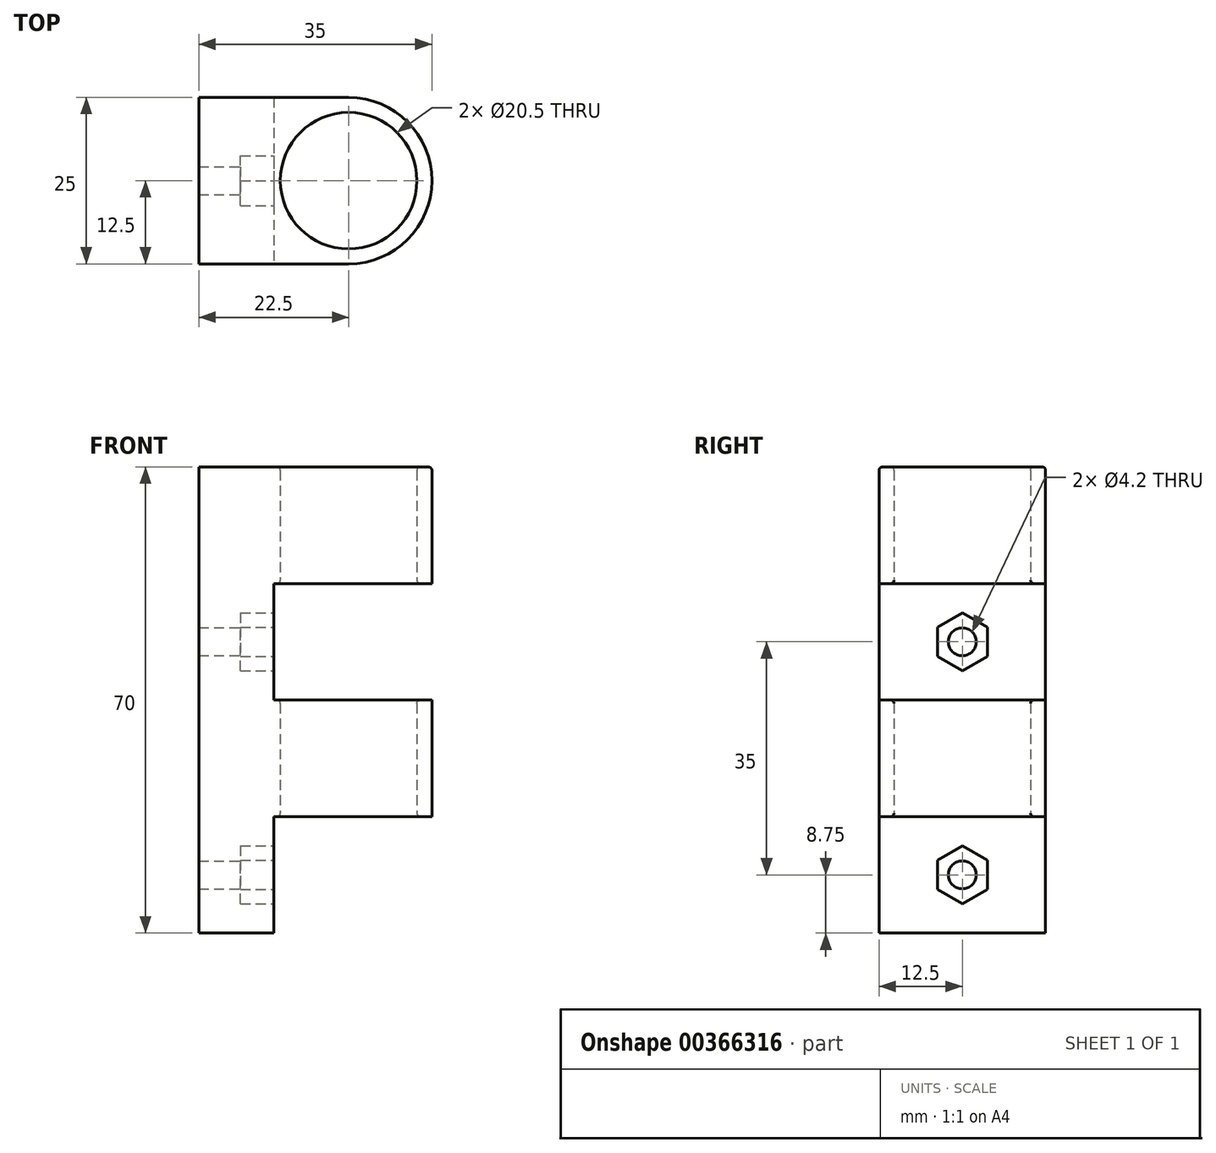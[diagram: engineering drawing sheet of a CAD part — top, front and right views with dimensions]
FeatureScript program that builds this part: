
annotation { "Feature Type Name" : "Feature", "Feature Type Description" : "" }
export const myFeature = defineFeature(function(context is Context, id is Id, definition is map)
    precondition{}
    {
        {
            var Q0;
            Q0=qCreatedBy(makeId("Top.planeOp"),FACE);
            var sketch = newSketch(context, id + "F0", { "sketchPlane" : qUnion([Q0])});
            skLineSegment(sketch, "E0.bottom", {"start": v(0, 0) * mm, "end": v(22.5, 0) * mm});
            skLineSegment(sketch, "E0.top", {"start": v(0, 25) * mm, "end": v(22.5, 25) * mm});
            skLineSegment(sketch, "E0.left", {"start": v(0, 0) * mm, "end": v(0, 25) * mm});
            skArc(sketch, "E1", {"start": v(22.5, 0) * mm, "mid": v(35, 12.5) * mm, "end": v(22.5, 25) * mm});
            skCircle(sketch, "E2", {"center": v(22.5, 12.5) * mm, "radius": 10.25 * mm});
            skSolve(sketch);
        }
        {
            var Q0;
            Q0=makeQuery(id+"F0.imprint","IMPRINT",FACE,{"disambiguationData":[TD([[makeQuery(id+"F0.imprint","IMPRINT",EDGE,{"derivedFrom":sQuery(id+"F0.wireOp",EDGE,"E0.bottom")}),1.0]])]});
            var Q1;
            Q1 = qSketchRegion(id + "F2", true);
            extrude(context, id + "F1", {"entities" : qUnion([Q0, Q1]), "depth" : 70 * mm});
        }
        {
            var Q0;
            Q0=makeQuery(id+"F1.opExtrude","SWEPT_FACE",FACE,{"disambiguationData":[OSD([sQuery(id+"F0.wireOp",EDGE,"E0.bottom")])]});
            var sketch = newSketch(context, id + "F2", { "sketchPlane" : qUnion([Q0])});
            skLineSegment(sketch, "E3", {"start": v(22.5, 35) * mm, "end": v(0, 35) * mm, "construction": true});
            skLineSegment(sketch, "E4.bottom", {"start": v(11.25, 35) * mm, "end": v(41.3, 35) * mm, "construction": true});
            skLineSegment(sketch, "E4.top", {"start": v(11.25, 52.5) * mm, "end": v(41.3, 52.5) * mm, "construction": true});
            skLineSegment(sketch, "E4.left", {"start": v(11.25, 35) * mm, "end": v(11.25, 52.5) * mm, "construction": true});
            skLineSegment(sketch, "E4.right", {"start": v(41.3, 35) * mm, "end": v(41.3, 52.5) * mm, "construction": true});
            skLineSegment(sketch, "E5", {"start": v(11.25, 35) * mm, "end": v(11.25, 0) * mm, "construction": true});
            skLineSegment(sketch, "E6.bottom", {"start": v(11.25, 0) * mm, "end": v(41.3, 0) * mm, "construction": true});
            skLineSegment(sketch, "E6.top", {"start": v(11.25, 17.5) * mm, "end": v(41.3, 17.5) * mm, "construction": true});
            skLineSegment(sketch, "E6.left", {"start": v(11.25, 0) * mm, "end": v(11.25, 17.5) * mm, "construction": true});
            skLineSegment(sketch, "E6.right", {"start": v(41.3, 0) * mm, "end": v(41.3, 17.5) * mm, "construction": true});
            skLineSegment(sketch, "E7.bottom", {"start": v(11.25, 52.5) * mm, "end": v(41.3, 52.5) * mm});
            skLineSegment(sketch, "E7.top", {"start": v(11.25, 35) * mm, "end": v(41.3, 35) * mm});
            skLineSegment(sketch, "E7.left", {"start": v(11.25, 52.5) * mm, "end": v(11.25, 35) * mm});
            skLineSegment(sketch, "E7.right", {"start": v(41.3, 52.5) * mm, "end": v(41.3, 35) * mm});
            skLineSegment(sketch, "E8.bottom", {"start": v(11.25, 17.5) * mm, "end": v(41.3, 17.5) * mm});
            skLineSegment(sketch, "E8.top", {"start": v(11.25, 0) * mm, "end": v(41.3, 0) * mm});
            skLineSegment(sketch, "E8.left", {"start": v(11.25, 17.5) * mm, "end": v(11.25, 0) * mm});
            skLineSegment(sketch, "E8.right", {"start": v(41.3, 17.5) * mm, "end": v(41.3, 0) * mm});
            skSolve(sketch);
        }
        {
            var Q0;
            {var subQ0=sQuery(id+"F2.wireOp",EDGE,"E8.left");Q0=makeQuery(id+"F2.imprint","IMPRINT",FACE,{"disambiguationData":[TD([[makeQuery(id+"F2.imprint","IMPRINT",EDGE,{"derivedFrom":subQ0}),1.0]])]});}
            var Q1;
            {var subQ0=sQuery(id+"F2.wireOp",EDGE,"E8.right");Q1=makeQuery(id+"F2.imprint","IMPRINT",FACE,{"disambiguationData":[TD([[makeQuery(id+"F2.imprint","IMPRINT",EDGE,{"derivedFrom":subQ0}),-1.0]])]});}
            var Q2;
            {var subQ0=sQuery(id+"F2.wireOp",EDGE,"E7.left");Q2=makeQuery(id+"F2.imprint","IMPRINT",FACE,{"disambiguationData":[TD([[makeQuery(id+"F2.imprint","IMPRINT",EDGE,{"derivedFrom":subQ0}),1.0]])]});}
            var Q3;
            {var subQ0=sQuery(id+"F2.wireOp",EDGE,"E7.right");Q3=makeQuery(id+"F2.imprint","IMPRINT",FACE,{"disambiguationData":[TD([[makeQuery(id+"F2.imprint","IMPRINT",EDGE,{"derivedFrom":subQ0}),-1.0]])]});}
            extrude(context, id + "F3", {"entities" : qUnion([Q0, Q1, Q2, Q3]), "operationType" : NewBodyOperationType.REMOVE, "oppositeDirection" : true, "depth" : 30 * mm});
        }
        {
            var Q0;
            Q0=makeQuery(id+"F3.boolean.opBoolean","COPY",FACE,{"derivedFrom":makeQuery(id+"F3.opExtrude","SWEPT_FACE",FACE,{"disambiguationData":[OSD([sQuery(id+"F2.wireOp",EDGE,"E7.left")])]})});
            var sketch = newSketch(context, id + "F4", { "sketchPlane" : qUnion([Q0])});
            skLineSegment(sketch, "E9", {"start": v(12.5, 52.5) * mm, "end": v(12.5, 35) * mm, "construction": true});
            skLineSegment(sketch, "E10", {"start": v(0, 43.75) * mm, "end": v(25, 43.75) * mm, "construction": true});
            skCircle(sketch, "E11", {"center": v(12.5, 43.75) * mm, "radius": 2.1 * mm});
            skCircle(sketch, "E12.cCircle", {"center": v(12.5, 43.75) * mm, "radius": 3.75 * mm, "construction": true});
            skLineSegment(sketch, "E12.0", {"start": v(16.25, 45.92) * mm, "end": v(16.25, 41.58) * mm});
            skLineSegment(sketch, "E12.1", {"start": v(16.25, 41.58) * mm, "end": v(12.5, 39.42) * mm});
            skLineSegment(sketch, "E12.2", {"start": v(12.5, 39.42) * mm, "end": v(8.75, 41.58) * mm});
            skLineSegment(sketch, "E12.3", {"start": v(8.75, 41.58) * mm, "end": v(8.75, 45.92) * mm});
            skLineSegment(sketch, "E12.4", {"start": v(8.75, 45.92) * mm, "end": v(12.5, 48.08) * mm});
            skLineSegment(sketch, "E12.5", {"start": v(12.5, 48.08) * mm, "end": v(16.25, 45.92) * mm});
            skPoint(sketch, "E12.0.midPoint", {"position": v(16.25, 43.75) * mm});
            skSolve(sketch);
        }
        {
            var Q0;
            Q0=makeQuery(id+"F4.imprint","IMPRINT",FACE,{"disambiguationData":[TD([[makeQuery(id+"F4.imprint","IMPRINT",EDGE,{"derivedFrom":sQuery(id+"F4.wireOp",EDGE,"E11")}),-1.0]])]});
            extrude(context, id + "F5", {"entities" : qUnion([Q0]), "operationType" : NewBodyOperationType.REMOVE, "oppositeDirection" : true, "depth" : 5 * mm});
        }
        {
            var Q0;
            Q0=makeQuery(id+"F5.boolean.opBoolean","SPLIT",FACE,{"disambiguationData":[TD([makeQuery(id+"F5.opExtrude","SWEPT_FACE",FACE,{"disambiguationData":[OSD([sQuery(id+"F4.wireOp",EDGE,"E11")])]})])],"derivedFrom":makeQuery(id+"F3.boolean.opBoolean","COPY",FACE,{"derivedFrom":makeQuery(id+"F3.opExtrude","SWEPT_FACE",FACE,{"disambiguationData":[OSD([sQuery(id+"F2.wireOp",EDGE,"E7.left")])]})})});
            extrude(context, id + "F6", {"entities" : qUnion([Q0]), "operationType" : NewBodyOperationType.REMOVE, "endBound" : BoundingType.THROUGH_ALL, "oppositeDirection" : true, "depth" : 25 * mm});
        }
        {
            var Q0;
            Q0=makeQuery(id+"F3.boolean.opBoolean","COPY",FACE,{"derivedFrom":makeQuery(id+"F3.opExtrude","SWEPT_FACE",FACE,{"disambiguationData":[OSD([sQuery(id+"F2.wireOp",EDGE,"E8.left")])]})});
            var sketch = newSketch(context, id + "F7", { "sketchPlane" : qUnion([Q0])});
            skLineSegment(sketch, "E13", {"start": v(12.5, 17.5) * mm, "end": v(12.5, 0) * mm, "construction": true});
            skLineSegment(sketch, "E14", {"start": v(0, 8.75) * mm, "end": v(25, 8.75) * mm, "construction": true});
            skCircle(sketch, "E15", {"center": v(12.5, 8.75) * mm, "radius": 2.1 * mm});
            skCircle(sketch, "E16.cCircle", {"center": v(12.5, 8.75) * mm, "radius": 3.75 * mm, "construction": true});
            skLineSegment(sketch, "E16.0", {"start": v(16.25, 10.92) * mm, "end": v(16.25, 6.58) * mm});
            skLineSegment(sketch, "E16.1", {"start": v(16.25, 6.58) * mm, "end": v(12.5, 4.42) * mm});
            skLineSegment(sketch, "E16.2", {"start": v(12.5, 4.42) * mm, "end": v(8.75, 6.58) * mm});
            skLineSegment(sketch, "E16.3", {"start": v(8.75, 6.58) * mm, "end": v(8.75, 10.92) * mm});
            skLineSegment(sketch, "E16.4", {"start": v(8.75, 10.92) * mm, "end": v(12.5, 13.08) * mm});
            skLineSegment(sketch, "E16.5", {"start": v(12.5, 13.08) * mm, "end": v(16.25, 10.92) * mm});
            skPoint(sketch, "E16.0.midPoint", {"position": v(16.25, 8.75) * mm});
            skSolve(sketch);
        }
        {
            var Q0;
            Q0=makeQuery(id+"F7.imprint","IMPRINT",FACE,{"disambiguationData":[TD([[makeQuery(id+"F7.imprint","IMPRINT",EDGE,{"derivedFrom":sQuery(id+"F7.wireOp",EDGE,"E15")}),-1.0]])]});
            extrude(context, id + "F8", {"entities" : qUnion([Q0]), "operationType" : NewBodyOperationType.REMOVE, "oppositeDirection" : true, "depth" : 5 * mm});
        }
        {
            var Q0;
            Q0=makeQuery(id+"F8.boolean.opBoolean","SPLIT",FACE,{"disambiguationData":[TD([makeQuery(id+"F8.opExtrude","SWEPT_FACE",FACE,{"disambiguationData":[OSD([sQuery(id+"F7.wireOp",EDGE,"E15")])]})])],"derivedFrom":makeQuery(id+"F3.boolean.opBoolean","COPY",FACE,{"derivedFrom":makeQuery(id+"F3.opExtrude","SWEPT_FACE",FACE,{"disambiguationData":[OSD([sQuery(id+"F2.wireOp",EDGE,"E8.left")])]})})});
            extrude(context, id + "F9", {"entities" : qUnion([Q0]), "operationType" : NewBodyOperationType.REMOVE, "endBound" : BoundingType.THROUGH_ALL, "oppositeDirection" : true, "depth" : 25 * mm});
        }
        {
            var Q0;
            Q0=makeQuery(id+"F3.boolean.opBoolean","COPY",EDGE,{"derivedFrom":makeQuery(id+"F3.opExtrude","CAP_EDGE",EDGE,{"disambiguationData":[OSD([sQuery(id+"F2.wireOp",EDGE,"E7.bottom")])],"isStart":true})});
            var Q1;
            Q1=makeQuery(id+"F3.boolean.opBoolean","COPY",EDGE,{"derivedFrom":makeQuery(id+"F3.opExtrude","CAP_EDGE",EDGE,{"disambiguationData":[OSD([sQuery(id+"F2.wireOp",EDGE,"E7.top")])],"isStart":true})});
            var Q2;
            Q2=makeQuery(id+"F3.boolean.opBoolean","COPY",EDGE,{"derivedFrom":makeQuery(id+"F3.opExtrude","CAP_EDGE",EDGE,{"disambiguationData":[OSD([sQuery(id+"F2.wireOp",EDGE,"E8.bottom")])],"isStart":true})});
            var Q3;
            Q3=makeQuery(id+"F3.boolean.opBoolean","INTERSECT",EDGE,{"derivedFrom":[makeQuery(id+"F1.opExtrude","SWEPT_FACE",FACE,{"disambiguationData":[OSD([sQuery(id+"F0.wireOp",EDGE,"E2")])]}),makeQuery(id+"F3.opExtrude","SWEPT_FACE",FACE,{"disambiguationData":[OSD([sQuery(id+"F2.wireOp",EDGE,"E8.bottom")])]})]});
            var Q4;
            Q4=makeQuery(id+"F3.boolean.opBoolean","INTERSECT",EDGE,{"derivedFrom":[makeQuery(id+"F1.opExtrude","SWEPT_FACE",FACE,{"disambiguationData":[OSD([sQuery(id+"F0.wireOp",EDGE,"E2")])]}),makeQuery(id+"F3.opExtrude","SWEPT_FACE",FACE,{"disambiguationData":[OSD([sQuery(id+"F2.wireOp",EDGE,"E7.top")])]})]});
            var Q5;
            Q5=makeQuery(id+"F3.boolean.opBoolean","INTERSECT",EDGE,{"derivedFrom":[makeQuery(id+"F1.opExtrude","SWEPT_FACE",FACE,{"disambiguationData":[OSD([sQuery(id+"F0.wireOp",EDGE,"E2")])]}),makeQuery(id+"F3.opExtrude","SWEPT_FACE",FACE,{"disambiguationData":[OSD([sQuery(id+"F2.wireOp",EDGE,"E7.bottom")])]})]});
            var Q6;
            Q6=makeQuery(id+"F1.opExtrude","CAP_EDGE",EDGE,{"disambiguationData":[OSD([sQuery(id+"F0.wireOp",EDGE,"E2")])],"isStart":false});
            var Q7;
            Q7=makeQuery(id+"F1.opExtrude","CAP_EDGE",EDGE,{"disambiguationData":[OSD([sQuery(id+"F0.wireOp",EDGE,"E1")])],"isStart":false});
            fillet(context, id + "F10", {"entities" : qUnion([Q0, Q1, Q2, Q3, Q4, Q5, Q6, Q7]), "radius" : 0.5 * mm, "tangentPropagation" : true, "allowEdgeOverflow" : false});
        }
    });
